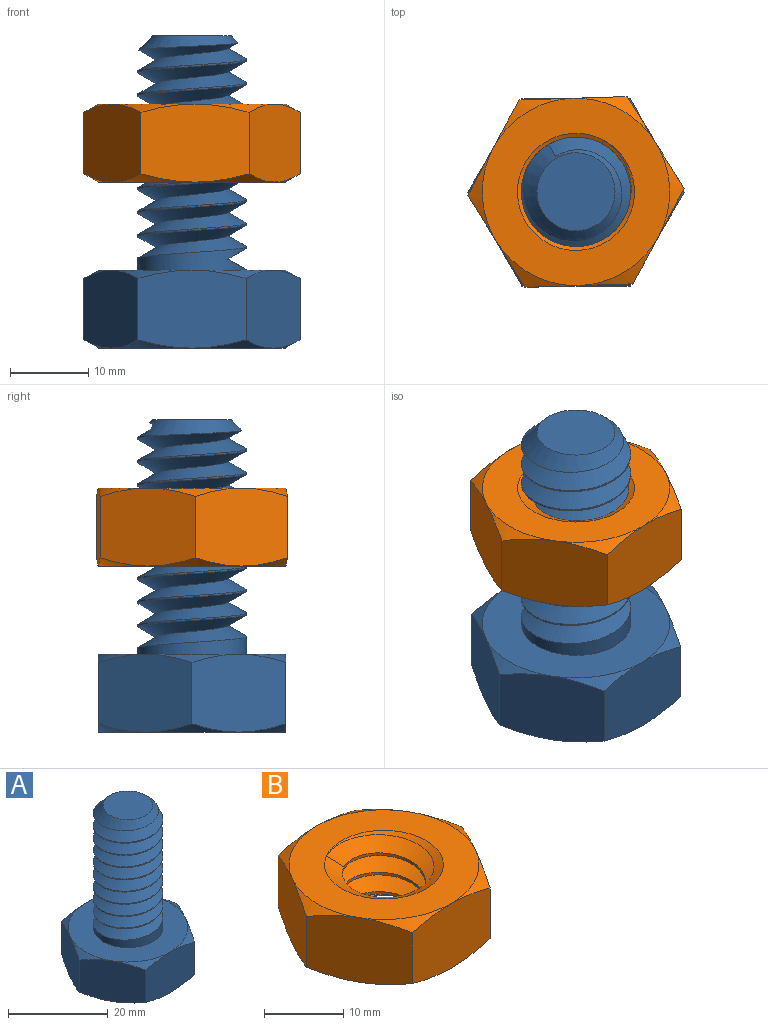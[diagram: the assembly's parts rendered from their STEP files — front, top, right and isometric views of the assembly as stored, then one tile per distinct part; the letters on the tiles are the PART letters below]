
ASSEMBLY  parts=2 mates=1
PART A: 28 faces, bbox 27.7x27.7x41.3 mm
  f0: cone r=7mm half-angle=45deg, axis (0,0,-1), area 59.4mm2, adj f1,f8,f23,f24
  f1: cylinder r=7mm len=28mm, axis (0,0,1), area 147.3mm2, adj f0,f9,f24,f25,f26,f27
  f2: cone r=17.5mm half-angle=60deg, axis (0,0,-1), area 8.9mm2, adj f9,f10,f15
  f3: cone r=17.5mm half-angle=60deg, axis (0,0,-1), area 8.9mm2, adj f9,f10,f11
  f4: cone r=17.5mm half-angle=60deg, axis (0,0,-1), area 8.9mm2, adj f9,f11,f12
  f5: cone r=17.5mm half-angle=60deg, axis (0,0,-1), area 8.9mm2, adj f9,f12,f13
  f6: cone r=17.5mm half-angle=60deg, axis (0,0,-1), area 8.9mm2, adj f9,f13,f14
  f7: cone r=17.5mm half-angle=60deg, axis (0,0,-1), area 8.9mm2, adj f9,f14,f15
  f8: plane 10x10mm, normal (0,0,1), area 78.5mm2, adj f0
  f9: plane 24x24mm, normal (0,0,1), area 298.5mm2, adj f1,f2,f3,f4,f5,f6,f7
  f10: plane 12x10.01mm, normal (0.87,0.5,0), area 128.4mm2, adj f2,f3,f11,f15,f19,f20
  f11: plane 12x10.01mm, normal (0.87,-0.5,0), area 128.4mm2, adj f3,f4,f10,f12,f18,f19
  f12: plane 13.87x10.01mm, normal (0,-1,0), area 128.4mm2, adj f4,f5,f11,f13,f17,f18
  f13: plane 12x10.01mm, normal (-0.87,-0.5,0), area 128.4mm2, adj f5,f6,f12,f14,f16,f17
  f14: plane 12x10.01mm, normal (-0.87,0.5,0), area 128.4mm2, adj f6,f7,f13,f15,f16,f22
  f15: plane 13.87x10.01mm, normal (0,1,0), area 128.4mm2, adj f2,f7,f10,f14,f20,f22
  f16: cone r=12mm half-angle=60deg, axis (0,0,1), area 8.9mm2, adj f13,f14,f21
  f17: cone r=12mm half-angle=60deg, axis (0,0,1), area 8.9mm2, adj f12,f13,f21
  f18: cone r=12mm half-angle=60deg, axis (0,0,1), area 8.9mm2, adj f11,f12,f21
  f19: cone r=12mm half-angle=60deg, axis (0,0,1), area 8.9mm2, adj f10,f11,f21
  f20: cone r=12mm half-angle=60deg, axis (0,0,1), area 8.9mm2, adj f10,f15,f21
  f21: plane 24x24mm, normal (0,0,-1), area 452.4mm2, adj f16,f17,f18,f19,f20,f22
  f22: cone r=12mm half-angle=60deg, axis (0,0,1), area 8.9mm2, adj f14,f15,f21
  f23: plane 2.1x1.78mm, normal (0.87,0.5,0), area 0.9mm2, adj f0,f24,f25
  f24: bspline ~29.9x16.17mm, area 915.4mm2, adj f0,f1,f23,f25,f26
  f25: bspline ~29.9x16.17mm, area 954.8mm2, adj f1,f23,f24,f27
  f26: plane 5.3x2.43mm, normal (0.5,0,-0.87), area 10.3mm2, adj f1,f24,f27
  f27: plane 5.3x2.43mm, normal (0.5,0,0.87), area 10.3mm2, adj f1,f25,f26
PART B: 25 faces, bbox 28.9x28.9x13.9 mm
  f0: cone r=7.5mm half-angle=60deg, axis (0,0,-1), area 61.6mm2, adj f1,f13,f23,f24
  f1: cylinder r=5.25mm len=10.5mm, axis (0,0,1), area 32.8mm2, adj f0,f14,f23,f24
  f2: cone r=12mm half-angle=60deg, axis (0,0,1), area 14.2mm2, adj f13,f17,f22
  f3: cone r=12mm half-angle=60deg, axis (0,0,1), area 14.2mm2, adj f13,f17,f18
  f4: cone r=12mm half-angle=60deg, axis (0,0,1), area 14.2mm2, adj f13,f18,f19
  f5: cone r=12mm half-angle=60deg, axis (0,0,1), area 14.2mm2, adj f13,f19,f20
  f6: cone r=12mm half-angle=60deg, axis (0,0,1), area 14.2mm2, adj f13,f20,f21
  f7: cone r=17.5mm half-angle=60deg, axis (0,0,-1), area 14.2mm2, adj f15,f19,f20
  f8: cone r=17.5mm half-angle=60deg, axis (0,0,-1), area 14.2mm2, adj f15,f18,f19
  f9: cone r=17.5mm half-angle=60deg, axis (0,0,-1), area 14.2mm2, adj f15,f17,f18
  f10: cone r=17.5mm half-angle=60deg, axis (0,0,-1), area 14.2mm2, adj f15,f20,f21
  f11: cone r=17.5mm half-angle=60deg, axis (0,0,-1), area 14.2mm2, adj f15,f17,f22
  f12: cone r=12mm half-angle=60deg, axis (0,0,1), area 14.2mm2, adj f13,f21,f22
  f13: plane 24x24mm, normal (0,0,-1), area 275.7mm2, adj f0,f2,f3,f4,f5,f6,f12
  f14: cone r=7.5mm half-angle=60deg, axis (0,0,1), area 61.7mm2, adj f1,f15,f23,f24
  f15: plane 24x24mm, normal (0,0,1), area 275.7mm2, adj f7,f8,f9,f10,f11,f14,f16
  f16: cone r=17.5mm half-angle=60deg, axis (0,0,-1), area 14.2mm2, adj f15,f21,f22
  f17: plane 13.14x11.14mm, normal (0.87,-0.5,0), area 128.4mm2, adj f2,f3,f9,f11,f18,f22
  f18: plane 15.01x11.15mm, normal (0,-1,0), area 128.4mm2, adj f3,f4,f8,f9,f17,f19
  f19: plane 13.14x11.14mm, normal (-0.87,-0.5,0), area 128.4mm2, adj f4,f5,f7,f8,f18,f20
  f20: plane 13.14x11.14mm, normal (-0.87,0.5,0), area 128.4mm2, adj f5,f6,f7,f10,f19,f21
  f21: plane 15.01x11.15mm, normal (0,1,0), area 128.4mm2, adj f6,f10,f12,f16,f20,f22
  f22: plane 13.14x11.14mm, normal (0.87,0.5,0), area 128.4mm2, adj f2,f11,f12,f16,f17,f21
  f23: bspline ~17.32x15mm, area 303.9mm2, adj f0,f1,f14,f24
  f24: bspline ~17.32x15mm, area 305.1mm2, adj f0,f1,f14,f23
PLACE A t=(0.03,-0.11,-7.43)mm fixed
PLACE B rot(axis=(0,0,-1),58.2deg) t=(-21.07,33.87,13.83)mm
MATE cylindrical A.f0 <-> B.f14  axis (0,0,1) through (0.03,-0.11,32.57)mm
